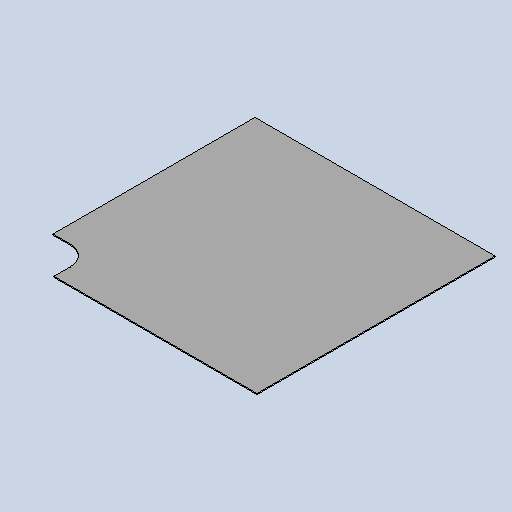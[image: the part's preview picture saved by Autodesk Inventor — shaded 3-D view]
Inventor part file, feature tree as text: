
AUTODESK INVENTOR PART (.ipt)
format: ipt  version: 2025.3 (Build 293356030, 356C)  size: 151,552 bytes
history: native  units: mm
features: other x2, sheet_metal_op x1, sketch x1
ambient origin geometry x8: Origin, YZ Plane, XZ Plane, XY Plane, X Axis, Y Axis, Z Axis, Center Point
bodies: Solid1 (feature_tree)
feature tree (4):
  sheet_metal_op  "Face1"
  sketch  "Sketch1"  dims[d2=479.0mm d3=2.0mm d18=475.0mm d21=40.0mm d22=72.0mm d23=74.0mm]
  other  "Plate1"
  other  "Definition1"
